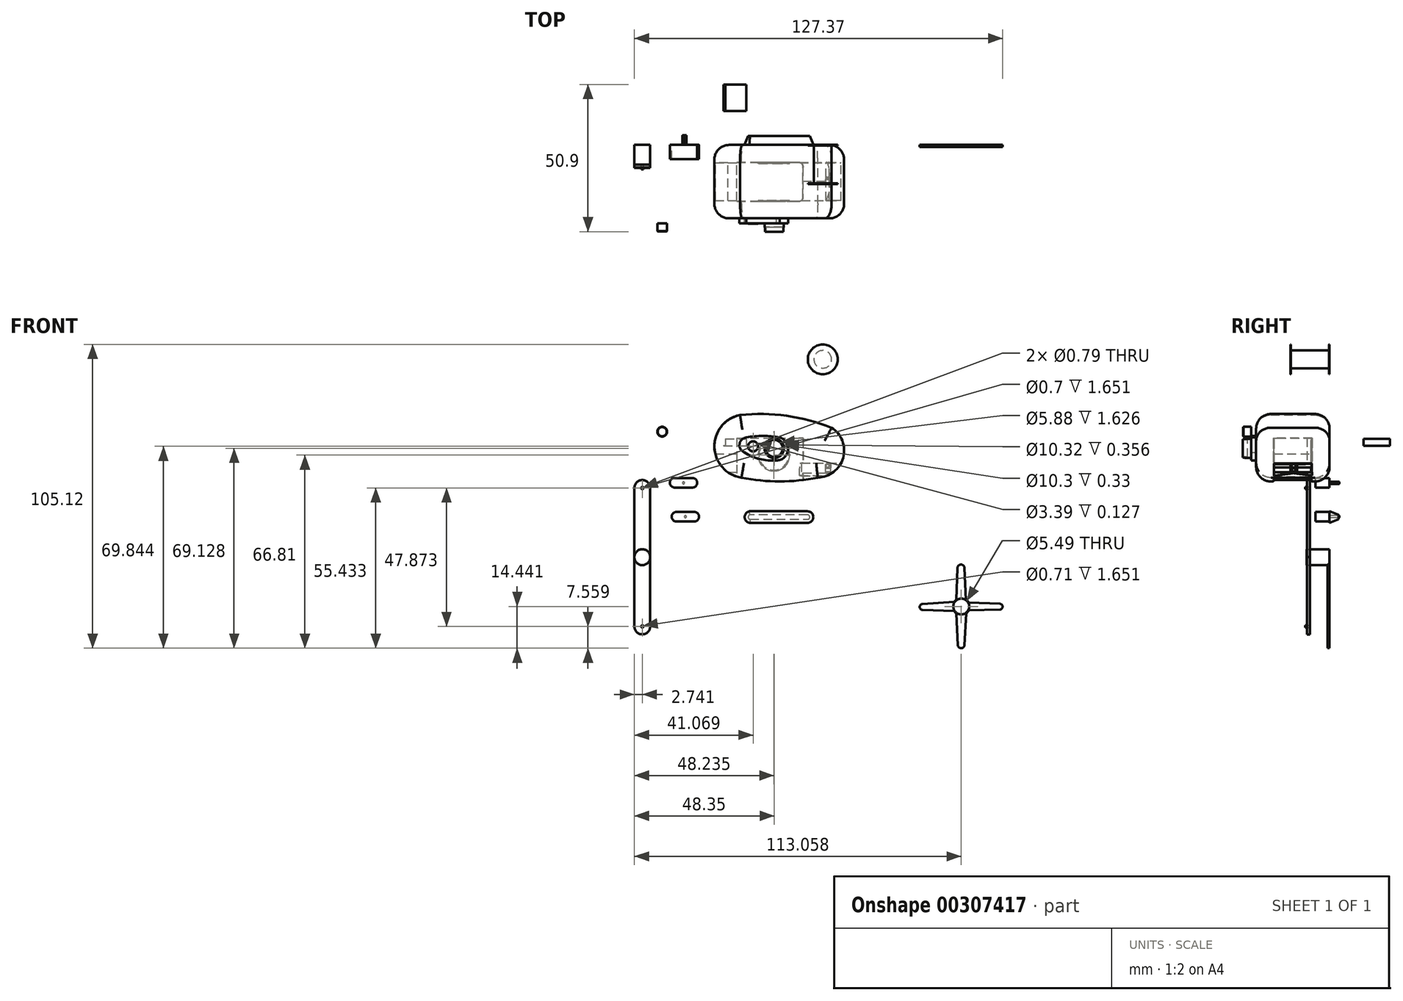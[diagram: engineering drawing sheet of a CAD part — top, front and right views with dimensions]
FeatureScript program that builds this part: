
annotation { "Feature Type Name" : "Feature", "Feature Type Description" : "" }
export const myFeature = defineFeature(function(context is Context, id is Id, definition is map)
    precondition{}
    {
        {
            var Q0;
            Q0=qCreatedBy(makeId("Front.planeOp"),FACE);
            var sketch = newSketch(context, id + "F0", { "sketchPlane" : qUnion([Q0])});
            skArc(sketch, "E0", {"start": v(-34.87, 37.31) * mm, "mid": v(-43.76, 26.28) * mm, "end": v(-34.38, 15.67) * mm});
            skArc(sketch, "E1", {"start": v(-3.21, 32.95) * mm, "mid": v(-18.78, 37.04) * mm, "end": v(-34.87, 37.31) * mm});
            skArc(sketch, "E2", {"start": v(-34.38, 15.67) * mm, "mid": v(-21.2, 14.34) * mm, "end": v(-8.02, 15.67) * mm});
            skArc(sketch, "E3", {"start": v(-8.02, 15.67) * mm, "mid": v(0.78, 22.53) * mm, "end": v(-3.21, 32.95) * mm});
            skSolve(sketch);
        }
        {
            var Q0;
            Q0=makeQuery(id+"F0.imprint","IMPRINT",FACE,{"disambiguationData":[TD([[makeQuery(id+"F0.imprint","IMPRINT",EDGE,{"derivedFrom":sQuery(id+"F0.wireOp",EDGE,"E0")}),1.0]])]});
            extrude(context, id + "F1", {"entities" : qUnion([Q0]), "depth" : 25.4 * mm});
        }
        {
            var Q0;
            Q0=makeQuery(id+"F1.opExtrude","CAP_FACE",FACE,{"disambiguationData":[OSD([sQuery(id+"F0.wireOp",EDGE,"E0"),sQuery(id+"F0.wireOp",EDGE,"E1"),sQuery(id+"F0.wireOp",EDGE,"E2"),sQuery(id+"F0.wireOp",EDGE,"E3")])],"isStart":false});
            var sketch = newSketch(context, id + "F2", { "sketchPlane" : qUnion([Q0])});
            skArc(sketch, "E4", {"start": v(-32.7, 29.56) * mm, "mid": v(-35.06, 27.22) * mm, "end": v(-33.35, 24.38) * mm});
            skArc(sketch, "E5", {"start": v(-21.2, 29.56) * mm, "mid": v(-26.95, 30.08) * mm, "end": v(-32.7, 29.56) * mm});
            skArc(sketch, "E6", {"start": v(-33.35, 24.38) * mm, "mid": v(-28.08, 22.09) * mm, "end": v(-22.35, 21.6) * mm});
            skArc(sketch, "E7", {"start": v(-22.35, 21.6) * mm, "mid": v(-18.29, 25.07) * mm, "end": v(-21.2, 29.56) * mm});
            skSolve(sketch);
        }
        {
            var Q0;
            Q0=makeQuery(id+"F2.imprint","IMPRINT",FACE,{"disambiguationData":[TD([[makeQuery(id+"F2.imprint","IMPRINT",EDGE,{"derivedFrom":sQuery(id+"F2.wireOp",EDGE,"E4")}),1.0]])]});
            extrude(context, id + "F3", {"entities" : qUnion([Q0]), "operationType" : NewBodyOperationType.ADD, "depth" : 1.7 * mm});
        }
        {
            var Q0;
            Q0=makeQuery(id+"F3.opExtrude","CAP_FACE",FACE,{"disambiguationData":[OSD([sQuery(id+"F2.wireOp",EDGE,"E4"),sQuery(id+"F2.wireOp",EDGE,"E5"),sQuery(id+"F2.wireOp",EDGE,"E6"),sQuery(id+"F2.wireOp",EDGE,"E7")])],"isStart":false});
            var sketch = newSketch(context, id + "F4", { "sketchPlane" : qUnion([Q0])});
            skCircle(sketch, "E8", {"center": v(-23.08, 25.77) * mm, "radius": 3.35 * mm});
            skCircle(sketch, "E9", {"center": v(-61.8, 31.56) * mm, "radius": 1.7 * mm});
            skSolve(sketch);
        }
        {
            var Q0;
            Q0=makeQuery(id+"F4.imprint","IMPRINT",FACE,{"disambiguationData":[TD([[makeQuery(id+"F4.imprint","IMPRINT",EDGE,{"derivedFrom":sQuery(id+"F4.wireOp",EDGE,"E8")}),1.0]])]});
            extrude(context, id + "F5", {"entities" : qUnion([Q0]), "operationType" : NewBodyOperationType.ADD, "depth" : 2.9 * mm, "hasDraft" : true, "draftAngle" : 3 * degree, "draftPullDirection" : true});
        }
        {
            var Q0;
            Q0=makeQuery(id+"F5.opExtrude","CAP_FACE",FACE,{"disambiguationData":[OSD([sQuery(id+"F4.wireOp",EDGE,"E8")])],"isStart":false});
            var sketch = newSketch(context, id + "F6", { "sketchPlane" : qUnion([Q0])});
            skCircle(sketch, "E10", {"center": v(-23.08, 25.77) * mm, "radius": 2.94 * mm});
            skSolve(sketch);
        }
        {
            var Q0;
            Q0=makeQuery(id+"F6.imprint","IMPRINT",FACE,{"disambiguationData":[TD([[makeQuery(id+"F6.imprint","IMPRINT",EDGE,{"derivedFrom":sQuery(id+"F6.wireOp",EDGE,"E10")}),1.0]])]});
            extrude(context, id + "F7", {"entities" : qUnion([Q0]), "operationType" : NewBodyOperationType.REMOVE, "oppositeDirection" : true, "depth" : 1.63 * mm});
        }
        {
            var Q0;
            Q0=makeQuery(id+"F4.imprint","IMPRINT",FACE,{"disambiguationData":[TD([[makeQuery(id+"F4.imprint","IMPRINT",EDGE,{"derivedFrom":sQuery(id+"F4.wireOp",EDGE,"E9")}),1.0]])]});
            extrude(context, id + "F8", {"entities" : qUnion([Q0]), "operationType" : NewBodyOperationType.ADD, "depth" : 2.72 * mm});
        }
        {
            var Q0;
            Q0=makeQuery(id+"F8.opExtrude","CAP_FACE",FACE,{"disambiguationData":[OSD([sQuery(id+"F4.wireOp",EDGE,"E9")])],"isStart":false});
            var sketch = newSketch(context, id + "F9", { "sketchPlane" : qUnion([Q0])});
            skCircle(sketch, "E11", {"center": v(-61.8, 31.56) * mm, "radius": 1.6 * mm});
            skSolve(sketch);
        }
        {
            var Q0;
            Q0 = qSketchRegion(id + "F9", true);
            extrude(context, id + "F10", {"entities" : qUnion([Q0]), "operationType" : NewBodyOperationType.ADD, "depth" : 0.1 * mm, "hasDraft" : true, "draftAngle" : 16 * degree, "draftPullDirection" : true});
        }
        {
            var Q0;
            Q0=makeQuery(id+"F1.opExtrude","CAP_EDGE",EDGE,{"disambiguationData":[OSD([sQuery(id+"F0.wireOp",EDGE,"E0")])],"isStart":false});
            var Q1;
            Q1=makeQuery(id+"F1.opExtrude","CAP_EDGE",EDGE,{"disambiguationData":[OSD([sQuery(id+"F0.wireOp",EDGE,"E2")])],"isStart":false});
            var Q2;
            Q2=makeQuery(id+"F1.opExtrude","CAP_EDGE",EDGE,{"disambiguationData":[OSD([sQuery(id+"F0.wireOp",EDGE,"E1")])],"isStart":false});
            var Q3;
            Q3=makeQuery(id+"F1.opExtrude","CAP_EDGE",EDGE,{"disambiguationData":[OSD([sQuery(id+"F0.wireOp",EDGE,"E3")])],"isStart":false});
            var Q4;
            Q4=makeQuery(id+"F1.opExtrude","CAP_EDGE",EDGE,{"disambiguationData":[OSD([sQuery(id+"F0.wireOp",EDGE,"E1")])],"isStart":true});
            var Q5;
            Q5=makeQuery(id+"F1.opExtrude","CAP_EDGE",EDGE,{"disambiguationData":[OSD([sQuery(id+"F0.wireOp",EDGE,"E3")])],"isStart":true});
            var Q6;
            Q6=makeQuery(id+"F1.opExtrude","CAP_EDGE",EDGE,{"disambiguationData":[OSD([sQuery(id+"F0.wireOp",EDGE,"E2")])],"isStart":true});
            var Q7;
            Q7=makeQuery(id+"F1.opExtrude","CAP_EDGE",EDGE,{"disambiguationData":[OSD([sQuery(id+"F0.wireOp",EDGE,"E0")])],"isStart":true});
            fillet(context, id + "F11", {"entities" : qUnion([Q0, Q1, Q2, Q3, Q4, Q5, Q6, Q7]), "radius" : 5.08 * mm, "tangentPropagation" : true, "allowEdgeOverflow" : false});
        }
        {
            var Q0;
            Q0=qCreatedBy(makeId("Top.planeOp"),FACE);
            var sketch = newSketch(context, id + "F12", { "sketchPlane" : qUnion([Q0])});
            skLineSegment(sketch, "E12", {"start": v(-35.98, -6.06) * mm, "end": v(-35.98, -19.55) * mm});
            skLineSegment(sketch, "E13", {"start": v(-35.98, -19.55) * mm, "end": v(-14.56, -19.55) * mm});
            skLineSegment(sketch, "E14", {"start": v(-35.98, -6.06) * mm, "end": v(-14.56, -6.06) * mm});
            skArc(sketch, "E15", {"start": v(-13.1, -7.76) * mm, "mid": v(-13.45, -6.57) * mm, "end": v(-14.56, -6.06) * mm});
            skArc(sketch, "E16", {"start": v(-14.56, -19.55) * mm, "mid": v(-13.53, -19.13) * mm, "end": v(-13.1, -18.1) * mm});
            skLineSegment(sketch, "E17", {"start": v(-13.1, -18.1) * mm, "end": v(-13.1, -7.76) * mm});
            skSolve(sketch);
        }
        {
            var Q0;
            Q0=makeQuery(id+"F12.imprint","IMPRINT",FACE,{"disambiguationData":[TD([[makeQuery(id+"F12.imprint","IMPRINT",EDGE,{"derivedFrom":sQuery(id+"F12.wireOp",EDGE,"E12")}),1.0]])]});
            extrude(context, id + "F13", {"entities" : qUnion([Q0]), "operationType" : NewBodyOperationType.REMOVE, "depth" : 29.3 * mm});
        }
        {
            var Q0;
            Q0=qCreatedBy(makeId("Right.planeOp"),FACE);
            var sketch = newSketch(context, id + "F14", { "sketchPlane" : qUnion([Q0])});
            skLineSegment(sketch, "E18", {"start": v(-6.08, 16.4) * mm, "end": v(-12.54, 17.23) * mm});
            skLineSegment(sketch, "E19", {"start": v(-12.54, 17.23) * mm, "end": v(-19.25, 16.26) * mm});
            skLineSegment(sketch, "E20", {"start": v(-19.25, 16.26) * mm, "end": v(-19.25, 20.69) * mm});
            skLineSegment(sketch, "E21", {"start": v(-19.25, 20.69) * mm, "end": v(-6.1, 20.69) * mm});
            skLineSegment(sketch, "E22", {"start": v(-6.1, 20.69) * mm, "end": v(-6.08, 16.4) * mm});
            skSolve(sketch);
        }
        {
            var Q0;
            Q0=makeQuery(id+"F14.imprint","IMPRINT",FACE,{"disambiguationData":[TD([[makeQuery(id+"F14.imprint","IMPRINT",EDGE,{"derivedFrom":sQuery(id+"F14.wireOp",EDGE,"E18")}),-1.0]])]});
            extrude(context, id + "F15", {"entities" : qUnion([Q0]), "operationType" : NewBodyOperationType.REMOVE, "oppositeDirection" : true, "depth" : 25.4 * mm});
        }
        {
            var Q0;
            Q0=qCreatedBy(makeId("Right.planeOp"),FACE);
            cPlane(context, id + "F16", {"entities" : qUnion([Q0]), "cplaneType" : CPlaneType.OFFSET, "offset" : 3.56 * mm, "oppositeDirection" : true, "width" : 152.4 * mm, "height" : 152.4 * mm});
        }
        {
            var Q0;
            Q0=makeQuery(id+"F15.boolean.opBoolean","COPY",FACE,{"derivedFrom":makeQuery(id+"F15.opExtrude","SWEPT_FACE",FACE,{"disambiguationData":[OSD([sQuery(id+"F14.wireOp",EDGE,"E22")])]})});
            var sketch = newSketch(context, id + "F17", { "sketchPlane" : qUnion([Q0])});
            skCircle(sketch, "E23", {"center": v(-4.6, 19.86) * mm, "radius": 0.58 * mm});
            skSolve(sketch);
        }
        {
            var Q0;
            Q0=makeQuery(id+"F17.imprint","IMPRINT",FACE,{"disambiguationData":[TD([[makeQuery(id+"F17.imprint","IMPRINT",EDGE,{"derivedFrom":sQuery(id+"F17.wireOp",EDGE,"E23")}),1.0]])]});
            extrude(context, id + "F18", {"entities" : qUnion([Q0]), "operationType" : NewBodyOperationType.ADD, "depth" : 13.72 * mm});
        }
        {
            var Q0;
            Q0=qCreatedBy(id+"F16.planeOp",FACE);
            var sketch = newSketch(context, id + "F19", { "sketchPlane" : qUnion([Q0])});
            skLineSegment(sketch, "E24", {"start": v(-11.19, 20.34) * mm, "end": v(-11.19, 17.2) * mm});
            skLineSegment(sketch, "E25", {"start": v(-11.19, 20.34) * mm, "end": v(-11.69, 20.34) * mm});
            skLineSegment(sketch, "E26", {"start": v(-11.69, 20.34) * mm, "end": v(-11.69, 17.26) * mm});
            skLineSegment(sketch, "E27", {"start": v(-13.57, 17.2) * mm, "end": v(-13.57, 20.34) * mm});
            skPoint(sketch, "E27.endSnap0", {"position": v(-11.44, 20.34) * mm});
            skLineSegment(sketch, "E28", {"start": v(-13.57, 20.34) * mm, "end": v(-13.18, 20.34) * mm});
            skLineSegment(sketch, "E29", {"start": v(-13.18, 20.34) * mm, "end": v(-13.18, 17.26) * mm});
            skCircle(sketch, "E30", {"center": v(-12.45, 18.33) * mm, "radius": 0.72 * mm});
            skCircle(sketch, "E31", {"center": v(-12.45, 18.33) * mm, "radius": 0.58 * mm});
            skLineSegment(sketch, "E32", {"start": v(-11.69, 17.58) * mm, "end": v(-13.18, 17.58) * mm});
            skLineSegment(sketch, "E33", {"start": v(-11.69, 19.02) * mm, "end": v(-13.18, 19.08) * mm});
            skLineSegment(sketch, "E34", {"start": v(-11.19, 17.2) * mm, "end": v(-11.69, 17.26) * mm});
            skLineSegment(sketch, "E35", {"start": v(-13.57, 17.2) * mm, "end": v(-13.18, 17.26) * mm});
            skSolve(sketch);
        }
        {
            var Q0;
            Q0=makeQuery(id+"F19.imprint","IMPRINT",FACE,{"disambiguationData":[TD([[makeQuery(id+"F19.imprint","IMPRINT",EDGE,{"derivedFrom":sQuery(id+"F19.wireOp",EDGE,"E27")}),-1.0]])]});
            var Q1;
            Q1=makeQuery(id+"F19.imprint","IMPRINT",FACE,{"disambiguationData":[TD([[makeQuery(id+"F19.imprint","IMPRINT",EDGE,{"derivedFrom":sQuery(id+"F19.wireOp",EDGE,"E24")}),-1.0]])]});
            var Q2;
            {var subQ1=sQuery(id+"F19.wireOp",EDGE,"E30");Q2=makeQuery(id+"F19.imprint","IMPRINT",FACE,{"disambiguationData":[TD([[makeQuery(id+"F19.imprint","IMPRINT",EDGE,{"derivedFrom":subQ1}),-1.0]])]});}
            var Q3;
            Q3=makeQuery(id+"F19.imprint","IMPRINT",FACE,{"disambiguationData":[TD([[makeQuery(id+"F19.imprint","IMPRINT",EDGE,{"derivedFrom":sQuery(id+"F19.wireOp",EDGE,"E30")}),1.0]])]});
            extrude(context, id + "F20", {"entities" : qUnion([Q0, Q1, Q2, Q3]), "operationType" : NewBodyOperationType.ADD, "oppositeDirection" : true, "depth" : 1.78 * mm});
        }
        {
            var Q0;
            Q0=makeQuery(id+"F1.opExtrude","SWEPT_FACE",FACE,{"disambiguationData":[OSD([sQuery(id+"F0.wireOp",EDGE,"E0")])]});
            var Q1;
            Q1=makeQuery(id+"F13.boolean.opBoolean","COPY",FACE,{"derivedFrom":makeQuery(id+"F13.opExtrude","SWEPT_FACE",FACE,{"disambiguationData":[OSD([sQuery(id+"F12.wireOp",EDGE,"E12")])]})});
            cPlane(context, id + "F21", {"entities" : qUnion([Q0, Q1]), "cplaneType" : CPlaneType.LINE_ANGLE, "offset" : 25.4 * mm, "angle" : 0 * degree, "width" : 152.4 * mm, "height" : 152.4 * mm});
        }
        {
            var Q0;
            Q0=qCreatedBy(id+"F21.planeOp",FACE);
            var sketch = newSketch(context, id + "F22", { "sketchPlane" : qUnion([Q0])});
            skLineSegment(sketch, "E36", {"start": v(19.23, 17.56) * mm, "end": v(6.14, 17.56) * mm});
            skLineSegment(sketch, "E37", {"start": v(6.14, 17.56) * mm, "end": v(6.14, 23.82) * mm});
            skLineSegment(sketch, "E38", {"start": v(6.14, 23.82) * mm, "end": v(19.23, 23.82) * mm});
            skLineSegment(sketch, "E39", {"start": v(19.23, 23.82) * mm, "end": v(19.23, 17.56) * mm});
            skSolve(sketch);
        }
        {
            var Q0;
            Q0=makeQuery(id+"F22.imprint","IMPRINT",FACE,{"disambiguationData":[TD([[makeQuery(id+"F22.imprint","IMPRINT",EDGE,{"derivedFrom":sQuery(id+"F22.wireOp",EDGE,"E36")}),-1.0]])]});
            extrude(context, id + "F23", {"entities" : qUnion([Q0]), "operationType" : NewBodyOperationType.REMOVE, "depth" : 25.4 * mm});
        }
        {
            var Q0;
            Q0=qCreatedBy(id+"F21.planeOp",FACE);
            var sketch = newSketch(context, id + "F24", { "sketchPlane" : qUnion([Q0])});
            skLineSegment(sketch, "E40", {"start": v(-11.76, 29.03) * mm, "end": v(-11.76, 26.63) * mm});
            skLineSegment(sketch, "E41", {"start": v(-11.76, 26.63) * mm, "end": v(-20.9, 26.63) * mm});
            skLineSegment(sketch, "E42", {"start": v(-20.9, 26.63) * mm, "end": v(-20.9, 29.03) * mm});
            skLineSegment(sketch, "E43", {"start": v(-20.9, 29.03) * mm, "end": v(-11.76, 29.03) * mm});
            skSolve(sketch);
        }
        {
            var Q0;
            Q0=makeQuery(id+"F24.imprint","IMPRINT",FACE,{"disambiguationData":[TD([[makeQuery(id+"F24.imprint","IMPRINT",EDGE,{"derivedFrom":sQuery(id+"F24.wireOp",EDGE,"E40")}),-1.0]])]});
            extrude(context, id + "F25", {"entities" : qUnion([Q0]), "depth" : 7.16 * mm});
        }
        {
            var Q0;
            Q0=makeQuery(id+"F25.opExtrude","CAP_FACE",FACE,{"disambiguationData":[OSD([sQuery(id+"F24.wireOp",EDGE,"E40"),sQuery(id+"F24.wireOp",EDGE,"E41"),sQuery(id+"F24.wireOp",EDGE,"E42"),sQuery(id+"F24.wireOp",EDGE,"E43")])],"isStart":false});
            var sketch = newSketch(context, id + "F26", { "sketchPlane" : qUnion([Q0])});
            skLineSegment(sketch, "E44", {"start": v(-11.76, 26.63) * mm, "end": v(-11.76, 26.82) * mm});
            skLineSegment(sketch, "E45", {"start": v(-11.76, 26.82) * mm, "end": v(-20.9, 26.82) * mm});
            skLineSegment(sketch, "E46", {"start": v(-20.9, 26.82) * mm, "end": v(-20.9, 26.63) * mm});
            skLineSegment(sketch, "E47", {"start": v(-20.9, 26.63) * mm, "end": v(-11.76, 26.63) * mm});
            skSolve(sketch);
        }
        {
            var Q0;
            Q0 = qSketchRegion(id + "F26", true);
            extrude(context, id + "F27", {"entities" : qUnion([Q0]), "operationType" : NewBodyOperationType.ADD, "depth" : 0.6 * mm});
        }
        {
            var Q0;
            Q0=makeQuery(id+"F13.boolean.opBoolean","COPY",FACE,{"derivedFrom":makeQuery(id+"F13.opExtrude","SWEPT_FACE",FACE,{"disambiguationData":[OSD([sQuery(id+"F12.wireOp",EDGE,"E13")])]})});
            var sketch = newSketch(context, id + "F28", { "sketchPlane" : qUnion([Q0])});
            skCircle(sketch, "E48", {"center": v(23.2, 23.45) * mm, "radius": 5.47 * mm});
            skCircle(sketch, "E49", {"center": v(23.2, 23.45) * mm, "radius": 5.15 * mm});
            skSolve(sketch);
        }
        {
            var Q0;
            Q0=makeQuery(id+"F13.boolean.opBoolean","COPY",FACE,{"derivedFrom":makeQuery(id+"F13.opExtrude","SWEPT_FACE",FACE,{"disambiguationData":[OSD([sQuery(id+"F12.wireOp",EDGE,"E14")])]})});
            var sketch = newSketch(context, id + "F29", { "sketchPlane" : qUnion([Q0])});
            skCircle(sketch, "E50", {"center": v(-23.2, 23.45) * mm, "radius": 5.49 * mm});
            skCircle(sketch, "E51", {"center": v(-23.2, 23.45) * mm, "radius": 5.16 * mm});
            skSolve(sketch);
        }
        {
            var Q0;
            Q0 = qSketchRegion(id + "F29", true);
            extrude(context, id + "F30", {"entities" : qUnion([Q0]), "operationType" : NewBodyOperationType.ADD, "depth" : 0.36 * mm});
        }
        {
            var Q0;
            Q0=makeQuery(id+"F28.imprint","IMPRINT",FACE,{"disambiguationData":[TD([[makeQuery(id+"F28.imprint","IMPRINT",EDGE,{"derivedFrom":sQuery(id+"F28.wireOp",EDGE,"E48")}),1.0]])]});
            extrude(context, id + "F31", {"entities" : qUnion([Q0]), "operationType" : NewBodyOperationType.ADD, "depth" : 0.33 * mm});
        }
        {
            var Q0;
            Q0=makeQuery(id+"F1.opExtrude","CAP_FACE",FACE,{"disambiguationData":[OSD([sQuery(id+"F0.wireOp",EDGE,"E0"),sQuery(id+"F0.wireOp",EDGE,"E1"),sQuery(id+"F0.wireOp",EDGE,"E2"),sQuery(id+"F0.wireOp",EDGE,"E3")])],"isStart":true});
            var sketch = newSketch(context, id + "F32", { "sketchPlane" : qUnion([Q0])});
            skCircle(sketch, "E52", {"center": v(6.26, 56.58) * mm, "radius": 5.16 * mm});
            skSolve(sketch);
        }
        {
            var Q0;
            Q0=makeQuery(id+"F32.imprint","IMPRINT",FACE,{"disambiguationData":[TD([[makeQuery(id+"F32.imprint","IMPRINT",EDGE,{"derivedFrom":sQuery(id+"F32.wireOp",EDGE,"E52")}),1.0]])]});
            extrude(context, id + "F33", {"entities" : qUnion([Q0]), "oppositeDirection" : true, "depth" : 0.15 * mm});
        }
        {
            var Q0;
            Q0=makeQuery(id+"F33.opExtrude","CAP_FACE",FACE,{"disambiguationData":[OSD([sQuery(id+"F32.wireOp",EDGE,"E52")])],"isStart":true});
            var sketch = newSketch(context, id + "F34", { "sketchPlane" : qUnion([Q0])});
            skCircle(sketch, "E53", {"center": v(6.26, 56.58) * mm, "radius": 3.06 * mm});
            skSolve(sketch);
        }
        {
            var Q0;
            Q0 = qSketchRegion(id + "F34", true);
            extrude(context, id + "F35", {"entities" : qUnion([Q0]), "operationType" : NewBodyOperationType.ADD, "oppositeDirection" : true, "depth" : 13.5 * mm});
        }
        {
            var Q0;
            Q0=makeQuery(id+"F35.opExtrude","CAP_FACE",FACE,{"disambiguationData":[OSD([sQuery(id+"F34.wireOp",EDGE,"E53")])],"isStart":false});
            var sketch = newSketch(context, id + "F36", { "sketchPlane" : qUnion([Q0])});
            skCircle(sketch, "E54", {"center": v(-6.26, 56.58) * mm, "radius": 5.17 * mm});
            skSolve(sketch);
        }
        {
            var Q0;
            Q0=makeQuery(id+"F36.imprint","IMPRINT",FACE,{"disambiguationData":[TD([[makeQuery(id+"F36.imprint","IMPRINT",EDGE,{"derivedFrom":sQuery(id+"F36.wireOp",EDGE,"E54")}),1.0]])]});
            extrude(context, id + "F37", {"entities" : qUnion([Q0]), "operationType" : NewBodyOperationType.ADD, "oppositeDirection" : true, "depth" : 0.15 * mm});
        }
        {
            var Q0;
            Q0=makeQuery(id+"F1.opExtrude","CAP_FACE",FACE,{"disambiguationData":[OSD([sQuery(id+"F0.wireOp",EDGE,"E0"),sQuery(id+"F0.wireOp",EDGE,"E1"),sQuery(id+"F0.wireOp",EDGE,"E2"),sQuery(id+"F0.wireOp",EDGE,"E3")])],"isStart":true});
            var sketch = newSketch(context, id + "F38", { "sketchPlane" : qUnion([Q0])});
            skArc(sketch, "E55", {"start": v(31.48, 0) * mm, "mid": v(33.3, 1.96) * mm, "end": v(31.58, 4) * mm});
            skLineSegment(sketch, "E56", {"start": v(31.48, 0) * mm, "end": v(11.54, 0) * mm});
            skLineSegment(sketch, "E57", {"start": v(31.58, 4) * mm, "end": v(11.54, 4) * mm});
            skArc(sketch, "E58", {"start": v(11.54, 4) * mm, "mid": v(9.54, 2) * mm, "end": v(11.54, 0) * mm});
            skSolve(sketch);
        }
        {
            var Q0;
            Q0=makeQuery(id+"F38.imprint","IMPRINT",FACE,{"disambiguationData":[TD([[makeQuery(id+"F38.imprint","IMPRINT",EDGE,{"derivedFrom":sQuery(id+"F38.wireOp",EDGE,"E55")}),1.0]])]});
            extrude(context, id + "F39", {"entities" : qUnion([Q0]), "depth" : 3.05 * mm, "hasDraft" : true, "draftAngle" : 22 * degree, "draftPullDirection" : true});
        }
        {
            var Q0;
            Q0=makeQuery(id+"F3.opExtrude","CAP_FACE",FACE,{"disambiguationData":[OSD([sQuery(id+"F2.wireOp",EDGE,"E4"),sQuery(id+"F2.wireOp",EDGE,"E5"),sQuery(id+"F2.wireOp",EDGE,"E6"),sQuery(id+"F2.wireOp",EDGE,"E7")])],"isStart":false});
            var sketch = newSketch(context, id + "F40", { "sketchPlane" : qUnion([Q0])});
            skCircle(sketch, "E59", {"center": v(-30.36, 26.48) * mm, "radius": 1.7 * mm});
            skCircle(sketch, "E60", {"center": v(-30.36, 26.48) * mm, "radius": 1.76 * mm});
            skSolve(sketch);
        }
        {
            var Q0;
            Q0 = qSketchRegion(id + "F40", true);
            extrude(context, id + "F41", {"entities" : qUnion([Q0]), "operationType" : NewBodyOperationType.ADD, "depth" : 0.13 * mm});
        }
        {
            var Q0;
            Q0=qCreatedBy(makeId("Front.planeOp"),FACE);
            var sketch = newSketch(context, id + "F42", { "sketchPlane" : qUnion([Q0])});
            skCircle(sketch, "E61", {"center": v(-68.69, -11.86) * mm, "radius": 2.75 * mm});
            skSolve(sketch);
        }
        {
            var Q0;
            Q0 = qSketchRegion(id + "F42", true);
            extrude(context, id + "F43", {"entities" : qUnion([Q0]), "depth" : 6.86 * mm});
        }
        {
            var Q0;
            Q0=makeQuery(id+"F43.opExtrude","CAP_FACE",FACE,{"disambiguationData":[OSD([sQuery(id+"F42.wireOp",EDGE,"E61")])],"isStart":false});
            var sketch = newSketch(context, id + "F44", { "sketchPlane" : qUnion([Q0])});
            skCircle(sketch, "E62", {"center": v(-68.69, -11.86) * mm, "radius": 2.75 * mm});
            skLineSegment(sketch, "E63", {"start": v(-71.43, -11.86) * mm, "end": v(-71.43, -35.8) * mm});
            skLineSegment(sketch, "E64", {"start": v(-65.94, -11.86) * mm, "end": v(-65.94, -35.8) * mm});
            skArc(sketch, "E65", {"start": v(-71.43, -35.8) * mm, "mid": v(-68.69, -38.55) * mm, "end": v(-65.94, -35.8) * mm});
            skLineSegment(sketch, "E66", {"start": v(-65.94, -11.86) * mm, "end": v(-65.94, 12.07) * mm});
            skLineSegment(sketch, "E67", {"start": v(-71.43, -11.86) * mm, "end": v(-71.43, 12.07) * mm});
            skArc(sketch, "E68", {"start": v(-65.94, 12.07) * mm, "mid": v(-68.69, 14.82) * mm, "end": v(-71.43, 12.07) * mm});
            skCircle(sketch, "E69", {"center": v(-68.69, -35.8) * mm, "radius": 0.4 * mm});
            skCircle(sketch, "E70", {"center": v(-68.69, 12.07) * mm, "radius": 0.4 * mm});
            skCircle(sketch, "E71", {"center": v(-68.69, 12.07) * mm, "radius": 0.35 * mm});
            skCircle(sketch, "E72", {"center": v(-68.69, -35.8) * mm, "radius": 0.36 * mm});
            skSolve(sketch);
        }
        {
            var Q0;
            {var subQ5=sQuery(id+"F44.wireOp",EDGE,"E65");Q0=makeQuery(id+"F44.imprint","IMPRINT",FACE,{"disambiguationData":[TD([[makeQuery(id+"F44.imprint","IMPRINT",EDGE,{"derivedFrom":subQ5}),1.0]])]});}
            var Q1;
            {var subQ0=makeQuery(id+"F43.opExtrude","CAP_EDGE",EDGE,{"disambiguationData":[OSD([sQuery(id+"F42.wireOp",EDGE,"E61")])],"isStart":false});var subQ1=makeQuery(id+"F44.imprint","INTERSECT",VERTEX,{"derivedFrom":[subQ0,sQuery(id+"F44.wireOp",EDGE,"E63"),sQuery(id+"F44.wireOp",EDGE,"E67")]});Q1=makeQuery(id+"F44.imprint","IMPRINT",FACE,{"disambiguationData":[TD([[makeQuery(id+"F44.imprint","IMPRINT",EDGE,{"disambiguationData":[TD([[subQ1,1.0]])],"derivedFrom":subQ0}),1.0]])]});}
            var Q2;
            {var subQ5=sQuery(id+"F44.wireOp",EDGE,"E68");Q2=makeQuery(id+"F44.imprint","IMPRINT",FACE,{"disambiguationData":[TD([[makeQuery(id+"F44.imprint","IMPRINT",EDGE,{"derivedFrom":subQ5}),1.0]])]});}
            extrude(context, id + "F45", {"entities" : qUnion([Q0, Q1, Q2]), "operationType" : NewBodyOperationType.ADD, "depth" : 1.02 * mm});
        }
        {
            var Q0;
            Q0=qCreatedBy(makeId("Front.planeOp"),FACE);
            var sketch = newSketch(context, id + "F46", { "sketchPlane" : qUnion([Q0])});
            skCircle(sketch, "E73", {"center": v(41.63, -28.92) * mm, "radius": 2.94 * mm});
            skLineSegment(sketch, "E74", {"start": v(41.63, -31.86) * mm, "end": v(41.63, -42.27) * mm});
            skLineSegment(sketch, "E75", {"start": v(44.57, -28.92) * mm, "end": v(54.98, -28.92) * mm});
            skLineSegment(sketch, "E76", {"start": v(41.63, -25.98) * mm, "end": v(41.63, -15.57) * mm});
            skLineSegment(sketch, "E77", {"start": v(38.69, -28.92) * mm, "end": v(28.28, -28.92) * mm});
            skLineSegment(sketch, "E78", {"start": v(43.34, -31.3) * mm, "end": v(42.75, -42.27) * mm});
            skLineSegment(sketch, "E79", {"start": v(39.92, -31.3) * mm, "end": v(40.45, -42.27) * mm});
            skLineSegment(sketch, "E80", {"start": v(44.25, -30.25) * mm, "end": v(54.98, -29.97) * mm});
            skLineSegment(sketch, "E81", {"start": v(44.25, -27.6) * mm, "end": v(54.98, -27.99) * mm});
            skLineSegment(sketch, "E82", {"start": v(43.29, -26.5) * mm, "end": v(42.74, -15.57) * mm});
            skLineSegment(sketch, "E83", {"start": v(39.97, -26.5) * mm, "end": v(40.33, -15.57) * mm});
            skLineSegment(sketch, "E84", {"start": v(39.17, -27.31) * mm, "end": v(28.28, -28.03) * mm});
            skLineSegment(sketch, "E85", {"start": v(39.17, -30.52) * mm, "end": v(28.28, -30.13) * mm});
            skArc(sketch, "E86", {"start": v(40.45, -42.27) * mm, "mid": v(41.6, -43.36) * mm, "end": v(42.75, -42.27) * mm});
            skArc(sketch, "E87", {"start": v(54.98, -29.97) * mm, "mid": v(55.94, -28.98) * mm, "end": v(54.98, -27.99) * mm});
            skArc(sketch, "E88", {"start": v(42.74, -15.57) * mm, "mid": v(41.54, -14.4) * mm, "end": v(40.33, -15.57) * mm});
            skArc(sketch, "E89", {"start": v(28.28, -28.03) * mm, "mid": v(27.27, -29.08) * mm, "end": v(28.28, -30.13) * mm});
            skCircle(sketch, "E90", {"center": v(41.63, -28.92) * mm, "radius": 2.75 * mm});
            skSolve(sketch);
        }
        {
            var Q0;
            Q0=makeQuery(id+"F43.opExtrude","CAP_FACE",FACE,{"disambiguationData":[OSD([sQuery(id+"F42.wireOp",EDGE,"E61")])],"isStart":false});
            extrude(context, id + "F47", {"entities" : qUnion([Q0]), "depth" : 1.07 * mm});
        }
        {
            var Q0;
            {var subQ0=sQuery(id+"F46.wireOp",EDGE,"E80");Q0=makeQuery(id+"F46.imprint","IMPRINT",FACE,{"disambiguationData":[TD([[makeQuery(id+"F46.imprint","IMPRINT",EDGE,{"derivedFrom":subQ0}),1.0]])]});}
            var Q1;
            {var subQ0=sQuery(id+"F46.wireOp",EDGE,"E78");Q1=makeQuery(id+"F46.imprint","IMPRINT",FACE,{"disambiguationData":[TD([[makeQuery(id+"F46.imprint","IMPRINT",EDGE,{"derivedFrom":subQ0}),-1.0]])]});}
            var Q2;
            {var subQ1=sQuery(id+"F46.wireOp",EDGE,"E84");Q2=makeQuery(id+"F46.imprint","IMPRINT",FACE,{"disambiguationData":[TD([[makeQuery(id+"F46.imprint","IMPRINT",EDGE,{"derivedFrom":subQ1}),1.0]])]});}
            var Q3;
            {var subQ0=sQuery(id+"F46.wireOp",EDGE,"E82");Q3=makeQuery(id+"F46.imprint","IMPRINT",FACE,{"disambiguationData":[TD([[makeQuery(id+"F46.imprint","IMPRINT",EDGE,{"derivedFrom":subQ0}),1.0]])]});}
            var Q4;
            Q4=makeQuery(id+"F46.imprint","IMPRINT",FACE,{"disambiguationData":[TD([[makeQuery(id+"F46.imprint","IMPRINT",EDGE,{"derivedFrom":sQuery(id+"F46.wireOp",EDGE,"E90")}),-1.0]])]});
            extrude(context, id + "F48", {"entities" : qUnion([Q0, Q1, Q2, Q3, Q4]), "depth" : 0.76 * mm});
        }
        {
            var Q0;
            Q0=makeQuery(id+"F44.imprint","IMPRINT",FACE,{"disambiguationData":[TD([[makeQuery(id+"F44.imprint","IMPRINT",EDGE,{"derivedFrom":sQuery(id+"F44.wireOp",EDGE,"E70")}),1.0]])]});
            var Q1;
            Q1=makeQuery(id+"F44.imprint","IMPRINT",FACE,{"disambiguationData":[TD([[makeQuery(id+"F44.imprint","IMPRINT",EDGE,{"derivedFrom":sQuery(id+"F44.wireOp",EDGE,"E69")}),1.0]])]});
            extrude(context, id + "F49", {"entities" : qUnion([Q0, Q1]), "depth" : 1.65 * mm});
        }
        {
            var Q0;
            Q0=qCreatedBy(makeId("Front.planeOp"),FACE);
            var sketch = newSketch(context, id + "F50", { "sketchPlane" : qUnion([Q0])});
            skCircle(sketch, "E91", {"center": v(-54.18, 13.77) * mm, "radius": 0.35 * mm});
            skLineSegment(sketch, "E92", {"start": v(-51.34, 12.23) * mm, "end": v(-57.51, 12.23) * mm});
            skLineSegment(sketch, "E93", {"start": v(-51.34, 15.54) * mm, "end": v(-57.51, 15.54) * mm});
            skArc(sketch, "E94", {"start": v(-51.34, 12.23) * mm, "mid": v(-49.68, 13.89) * mm, "end": v(-51.34, 15.54) * mm});
            skArc(sketch, "E95", {"start": v(-57.51, 15.54) * mm, "mid": v(-59.17, 13.89) * mm, "end": v(-57.51, 12.23) * mm});
            skCircle(sketch, "E96", {"center": v(-53.54, 2.01) * mm, "radius": 0.35 * mm});
            skLineSegment(sketch, "E97", {"start": v(-50.7, 0.48) * mm, "end": v(-56.88, 0.48) * mm});
            skLineSegment(sketch, "E98", {"start": v(-50.7, 3.79) * mm, "end": v(-56.88, 3.79) * mm});
            skArc(sketch, "E99", {"start": v(-50.7, 0.48) * mm, "mid": v(-49.04, 2.14) * mm, "end": v(-50.7, 3.79) * mm});
            skArc(sketch, "E100", {"start": v(-56.88, 3.79) * mm, "mid": v(-58.53, 2.14) * mm, "end": v(-56.88, 0.48) * mm});
            skSolve(sketch);
        }
        {
            var Q0;
            Q0=makeQuery(id+"F50.imprint","IMPRINT",FACE,{"disambiguationData":[TD([[makeQuery(id+"F50.imprint","IMPRINT",EDGE,{"derivedFrom":sQuery(id+"F50.wireOp",EDGE,"E91")}),-1.0]])]});
            var Q1;
            Q1=makeQuery(id+"F50.imprint","IMPRINT",FACE,{"disambiguationData":[TD([[makeQuery(id+"F50.imprint","IMPRINT",EDGE,{"derivedFrom":sQuery(id+"F50.wireOp",EDGE,"E91")}),1.0]])]});
            extrude(context, id + "F51", {"entities" : qUnion([Q0, Q1]), "depth" : 4.95 * mm});
        }
        {
            var Q0;
            Q0=makeQuery(id+"F51.opExtrude","CAP_FACE",FACE,{"disambiguationData":[OSD([sQuery(id+"F50.wireOp",EDGE,"E92"),sQuery(id+"F50.wireOp",EDGE,"E93"),sQuery(id+"F50.wireOp",EDGE,"E94"),sQuery(id+"F50.wireOp",EDGE,"E95")])],"isStart":true});
            var sketch = newSketch(context, id + "F52", { "sketchPlane" : qUnion([Q0])});
            skCircle(sketch, "E101", {"center": v(54.43, 13.85) * mm, "radius": 0.35 * mm});
            skPoint(sketch, "E101.centerSnap0", {"position": v(54.43, 12.23) * mm});
            skSolve(sketch);
        }
        {
            var Q0;
            Q0=makeQuery(id+"F52.imprint","IMPRINT",FACE,{"disambiguationData":[TD([[makeQuery(id+"F52.imprint","IMPRINT",EDGE,{"derivedFrom":sQuery(id+"F52.wireOp",EDGE,"E101")}),1.0]])]});
            extrude(context, id + "F53", {"entities" : qUnion([Q0]), "operationType" : NewBodyOperationType.ADD, "depth" : 3.3 * mm});
        }
        {
            var Q0;
            Q0=makeQuery(id+"F50.imprint","IMPRINT",FACE,{"disambiguationData":[TD([[makeQuery(id+"F50.imprint","IMPRINT",EDGE,{"derivedFrom":sQuery(id+"F50.wireOp",EDGE,"E96")}),1.0]])]});
            var Q1;
            Q1=makeQuery(id+"F50.imprint","IMPRINT",FACE,{"disambiguationData":[TD([[makeQuery(id+"F50.imprint","IMPRINT",EDGE,{"derivedFrom":sQuery(id+"F50.wireOp",EDGE,"E96")}),-1.0]])]});
            extrude(context, id + "F54", {"entities" : qUnion([Q0, Q1]), "depth" : 4.95 * mm});
        }
        {
            var Q0;
            Q0=makeQuery(id+"F54.opExtrude","CAP_FACE",FACE,{"disambiguationData":[OSD([sQuery(id+"F50.wireOp",EDGE,"E97"),sQuery(id+"F50.wireOp",EDGE,"E98"),sQuery(id+"F50.wireOp",EDGE,"E99"),sQuery(id+"F50.wireOp",EDGE,"E100")])],"isStart":true});
            var sketch = newSketch(context, id + "F55", { "sketchPlane" : qUnion([Q0])});
            skCircle(sketch, "E102", {"center": v(53.79, 2.16) * mm, "radius": 0.35 * mm});
            skPoint(sketch, "E102.centerSnap0", {"position": v(53.79, 3.79) * mm});
            skSolve(sketch);
        }
        {
            var Q0;
            Q0=makeQuery(id+"F55.imprint","IMPRINT",FACE,{"disambiguationData":[TD([[makeQuery(id+"F55.imprint","IMPRINT",EDGE,{"derivedFrom":sQuery(id+"F55.wireOp",EDGE,"E102")}),1.0]])]});
            extrude(context, id + "F56", {"entities" : qUnion([Q0]), "operationType" : NewBodyOperationType.ADD, "depth" : 3.3 * mm});
        }
    });
